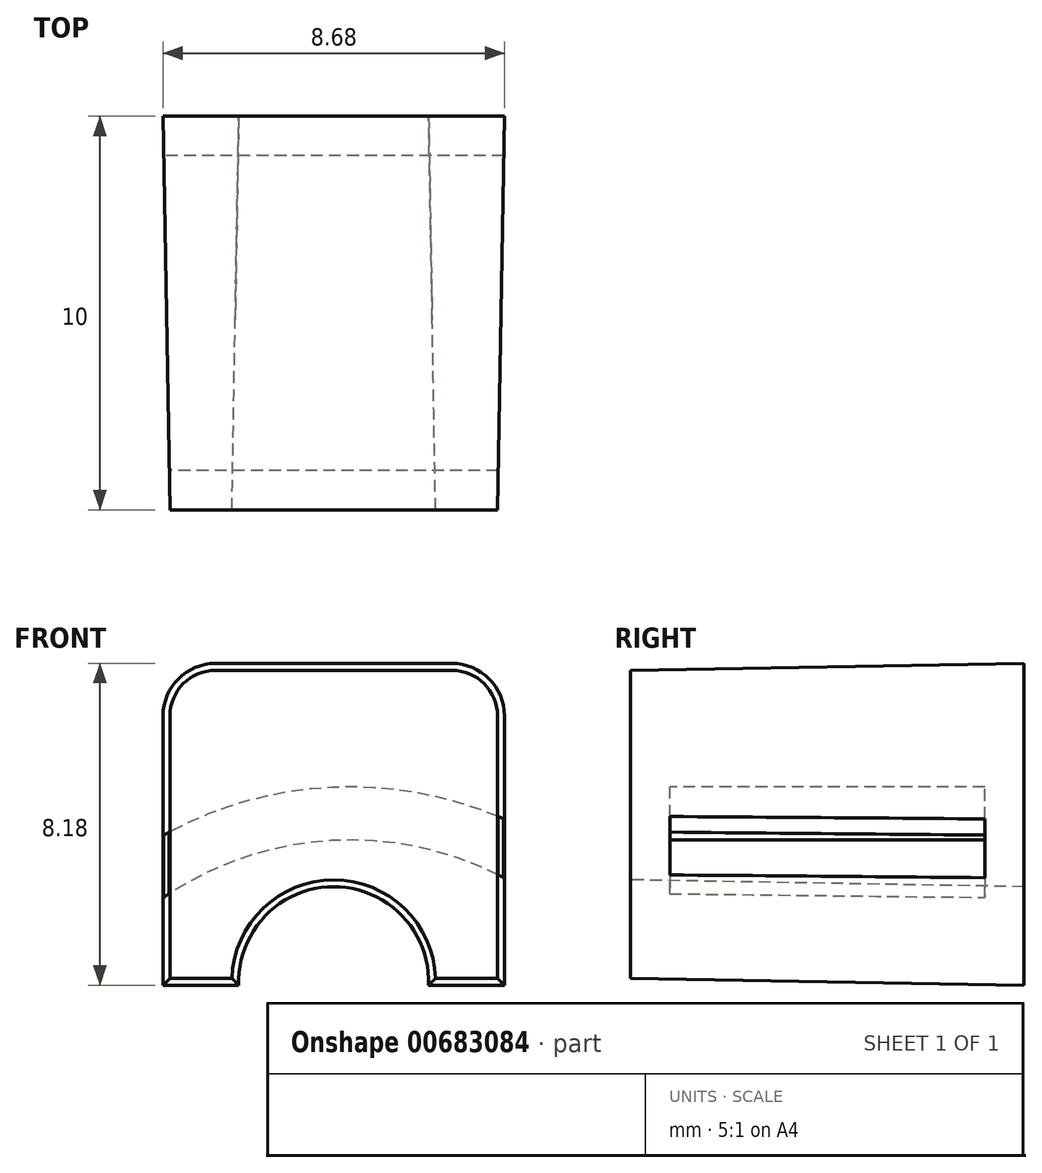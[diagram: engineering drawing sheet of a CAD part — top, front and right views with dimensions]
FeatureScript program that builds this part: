
annotation { "Feature Type Name" : "Feature", "Feature Type Description" : "" }
export const myFeature = defineFeature(function(context is Context, id is Id, definition is map)
    precondition{}
    {
        {
            var Q0;
            Q0=qCreatedBy(makeId("Front.planeOp"),FACE);
            var sketch = newSketch(context, id + "F0", { "sketchPlane" : qUnion([Q0])});
            skArc(sketch, "E0", {"start": v(-2.5, 0) * mm, "mid": v(0, 2.5) * mm, "end": v(2.5, 0) * mm});
            skLineSegment(sketch, "E1", {"start": v(2.5, 0) * mm, "end": v(4.25, 0) * mm});
            skLineSegment(sketch, "E2", {"start": v(4.25, 0) * mm, "end": v(4.25, 6.75) * mm});
            skLineSegment(sketch, "E3", {"start": v(3, 8) * mm, "end": v(-3, 8) * mm});
            skLineSegment(sketch, "E4", {"start": v(-4.25, 6.75) * mm, "end": v(-4.25, 0) * mm});
            skLineSegment(sketch, "E5", {"start": v(-4.25, 0) * mm, "end": v(-2.5, 0) * mm});
            skPoint(sketch, "E6.visualSharp", {"position": v(-4.25, 8) * mm});
            skArc(sketch, "E6.filletArc", {"start": v(-3, 8) * mm, "mid": v(-3.88, 7.63) * mm, "end": v(-4.25, 6.75) * mm});
            skPoint(sketch, "E7.visualSharp", {"position": v(4.25, 8) * mm});
            skArc(sketch, "E7.filletArc", {"start": v(4.25, 6.75) * mm, "mid": v(3.88, 7.63) * mm, "end": v(3, 8) * mm});
            skSolve(sketch);
        }
        {
            var Q0;
            Q0 = qSketchRegion(id + "F0", true);
            extrude(context, id + "F1", {"entities" : qUnion([Q0]), "depth" : 5 * mm, "offsetDistance" : 25 * mm, "hasDraft" : true, "draftAngle" : 1 * degree, "draftPullDirection" : true, "hasSecondDirection" : true, "secondDirectionOppositeDirection" : true, "secondDirectionDepth" : 5 * mm, "hasSecondDirectionDraft" : true, "secondDirectionDraftAngle" : 1 * degree});
        }
        {
            var Q0;
            Q0=qCreatedBy(makeId("Front.planeOp"),FACE);
            var sketch = newSketch(context, id + "F2", { "sketchPlane" : qUnion([Q0])});
            skArc(sketch, "E8", {"start": v(7.54, 1.87) * mm, "mid": v(0.6, 4.95) * mm, "end": v(-6.45, 2.13) * mm});
            skArc(sketch, "E9.0", {"start": v(6.47, 1.04) * mm, "mid": v(0.57, 3.6) * mm, "end": v(-5.42, 1.25) * mm});
            skLineSegment(sketch, "E10", {"start": v(-5.42, 1.25) * mm, "end": v(-6.45, 2.13) * mm});
            skLineSegment(sketch, "E11", {"start": v(6.47, 1.04) * mm, "end": v(7.54, 1.87) * mm});
            skSolve(sketch);
        }
        {
            var Q0;
            Q0=makeQuery(id+"F2.imprint","IMPRINT",FACE,{"disambiguationData":[TD([[makeQuery(id+"F2.imprint","IMPRINT",EDGE,{"derivedFrom":sQuery(id+"F2.wireOp",EDGE,"E8")}),1.0]])]});
            extrude(context, id + "F3", {"entities" : qUnion([Q0]), "operationType" : NewBodyOperationType.REMOVE, "oppositeDirection" : true, "depth" : 4 * mm, "offsetDistance" : 25 * mm, "hasSecondDirection" : true, "secondDirectionOppositeDirection" : false, "secondDirectionDepth" : 4 * mm});
        }
    });
